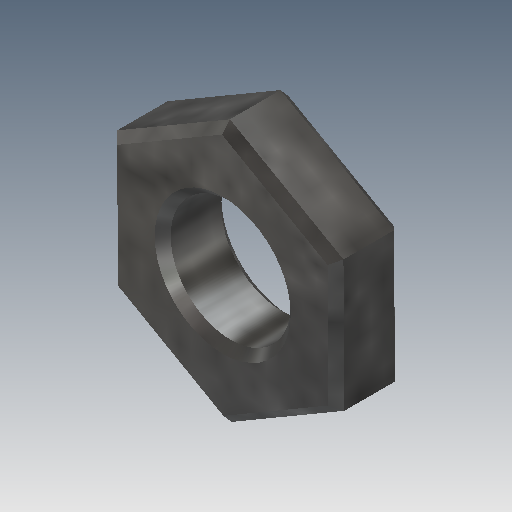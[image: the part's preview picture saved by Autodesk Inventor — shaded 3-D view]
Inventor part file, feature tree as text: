
AUTODESK INVENTOR PART (.ipt)
format: ipt  version: 2018 (Build 220112000, 112)  size: 160,768 bytes
history: native  units: mm
features: extrude x1, chamfer x1, sketch x1
ambient origin geometry x8: Origin, YZ Plane, XZ Plane, XY Plane, X Axis, Y Axis, Z Axis, Center Point
bodies: Solid1 (feature_tree)
feature tree (3):
  extrude  "Extrusion1"  Depth=5.0mm
  chamfer  "Chamfer1"  Distance=5.0mm
  sketch  "Sketch1"  dims[d0=9.02mm d1=8.5mm d2=5.0mm d3=0.0mm d4=0.6mm d5=2.0mm d6=45.0deg]
